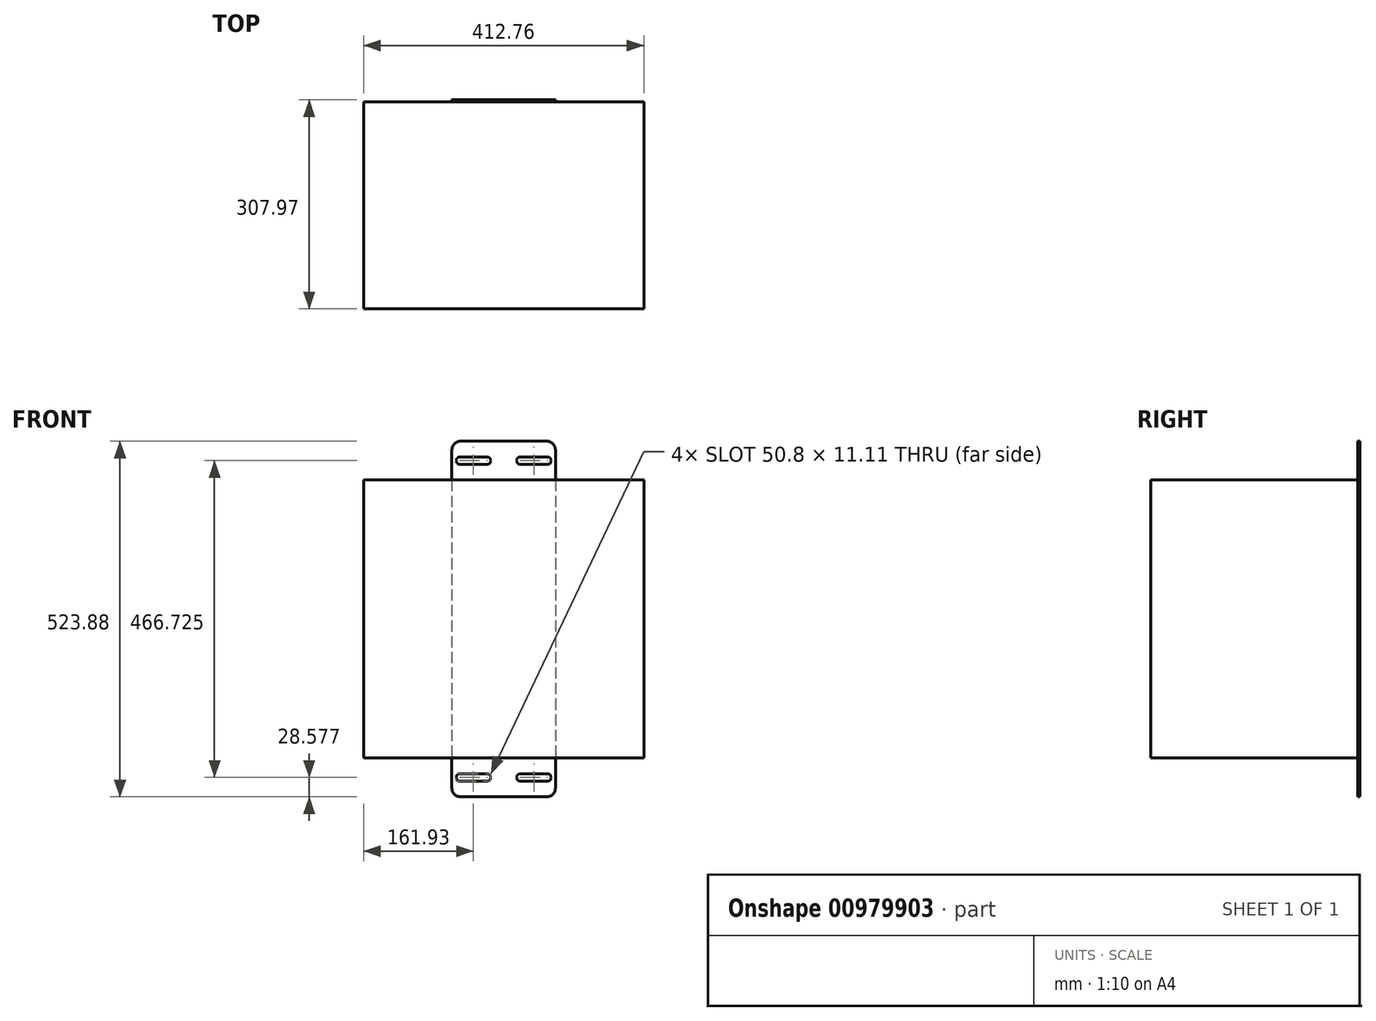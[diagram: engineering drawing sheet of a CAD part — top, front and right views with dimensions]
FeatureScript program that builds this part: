
annotation { "Feature Type Name" : "Feature", "Feature Type Description" : "" }
export const myFeature = defineFeature(function(context is Context, id is Id, definition is map)
    precondition{}
    {
        {
            var Q0;
            Q0=qCreatedBy(makeId("Top.planeOp"),FACE);
            var sketch = newSketch(context, id + "F0", { "sketchPlane" : qUnion([Q0])});
            skLineSegment(sketch, "E0.bottom", {"start": v(206.38, 152.4) * mm, "end": v(-206.38, 152.4) * mm});
            skLineSegment(sketch, "E0.top", {"start": v(206.38, -152.4) * mm, "end": v(-206.38, -152.4) * mm});
            skLineSegment(sketch, "E0.left", {"start": v(206.38, 152.4) * mm, "end": v(206.38, -152.4) * mm});
            skLineSegment(sketch, "E0.right", {"start": v(-206.38, 152.4) * mm, "end": v(-206.38, -152.4) * mm});
            skPoint(sketch, "E0.middle", {"position": v(0, 0) * mm});
            skSolve(sketch);
        }
        {
            var Q0;
            Q0=qSketchRegion(id+"F0",true);
            extrude(context, id + "F1", {"entities" : qUnion([Q0]), "depth" : 409.57 * mm, "offsetDistance" : 25.4 * mm, "symmetric" : true});
        }
        {
            var Q0;
            Q0=makeQuery(id+"F1.opExtrude","SWEPT_FACE",FACE,{"disambiguationData":[OSD([sQuery(id+"F0.wireOp",EDGE,"E0.bottom")])]});
            var sketch = newSketch(context, id + "F2", { "sketchPlane" : qUnion([Q0])});
            skLineSegment(sketch, "E1.bottom", {"start": v(63.5, 261.94) * mm, "end": v(-63.5, 261.94) * mm});
            skLineSegment(sketch, "E1.top", {"start": v(63.5, -261.94) * mm, "end": v(-63.5, -261.94) * mm});
            skLineSegment(sketch, "E1.left", {"start": v(76.2, 249.24) * mm, "end": v(76.2, -249.24) * mm});
            skLineSegment(sketch, "E1.right", {"start": v(-76.2, 249.24) * mm, "end": v(-76.2, -249.24) * mm});
            skPoint(sketch, "E1.middle", {"position": v(0, 0) * mm});
            skLineSegment(sketch, "E2", {"start": v(-76.2, 0) * mm, "end": v(76.2, 0) * mm, "construction": true});
            skLineSegment(sketch, "E3.0", {"start": v(-206.38, 204.79) * mm, "end": v(206.38, 204.79) * mm, "construction": true});
            skPoint(sketch, "E4.visualSharp", {"position": v(-76.2, 261.94) * mm});
            skArc(sketch, "E4.filletArc", {"start": v(-63.5, 261.94) * mm, "mid": v(-72.48, 258.22) * mm, "end": v(-76.2, 249.24) * mm});
            skPoint(sketch, "E5.visualSharp", {"position": v(76.2, 261.94) * mm});
            skArc(sketch, "E5.filletArc", {"start": v(76.2, 249.24) * mm, "mid": v(72.48, 258.22) * mm, "end": v(63.5, 261.94) * mm});
            skPoint(sketch, "E6.visualSharp", {"position": v(-76.2, -261.94) * mm});
            skArc(sketch, "E6.filletArc", {"start": v(-76.2, -249.24) * mm, "mid": v(-72.48, -258.22) * mm, "end": v(-63.5, -261.94) * mm});
            skPoint(sketch, "E7.visualSharp", {"position": v(76.2, -261.94) * mm});
            skArc(sketch, "E7.filletArc", {"start": v(63.5, -261.94) * mm, "mid": v(72.48, -258.22) * mm, "end": v(76.2, -249.24) * mm});
            skLineSegment(sketch, "E8", {"start": v(0, 261.94) * mm, "end": v(0, 204.79) * mm, "construction": true});
            skLineSegment(sketch, "E9", {"start": v(-76.2, 233.36) * mm, "end": v(76.2, 233.36) * mm, "construction": true});
            skPoint(sketch, "E9.startSnap0", {"position": v(0, 233.36) * mm});
            skLineSegment(sketch, "E10.bottom", {"start": v(64.3, 238.92) * mm, "end": v(24.6, 238.92) * mm});
            skLineSegment(sketch, "E10.top", {"start": v(64.3, 227.8) * mm, "end": v(24.6, 227.8) * mm});
            skLineSegment(sketch, "E10.left", {"start": v(64.3, 238.92) * mm, "end": v(64.3, 227.8) * mm, "construction": true});
            skLineSegment(sketch, "E10.right", {"start": v(24.6, 238.92) * mm, "end": v(24.6, 227.8) * mm, "construction": true});
            skPoint(sketch, "E10.middle", {"position": v(44.45, 233.36) * mm});
            skLineSegment(sketch, "E11.bottom", {"start": v(-24.6, 238.92) * mm, "end": v(-64.3, 238.92) * mm});
            skLineSegment(sketch, "E11.top", {"start": v(-24.6, 227.8) * mm, "end": v(-64.3, 227.8) * mm});
            skLineSegment(sketch, "E11.left", {"start": v(-24.6, 238.92) * mm, "end": v(-24.6, 227.8) * mm, "construction": true});
            skLineSegment(sketch, "E11.right", {"start": v(-64.3, 238.92) * mm, "end": v(-64.3, 227.8) * mm, "construction": true});
            skPoint(sketch, "E11.middle", {"position": v(-44.45, 233.36) * mm});
            skArc(sketch, "E12", {"start": v(-64.3, 238.92) * mm, "mid": v(-69.85, 233.36) * mm, "end": v(-64.3, 227.8) * mm});
            skArc(sketch, "E13", {"start": v(-24.6, 227.8) * mm, "mid": v(-19.05, 233.36) * mm, "end": v(-24.6, 238.92) * mm});
            skArc(sketch, "E14", {"start": v(24.6, 238.92) * mm, "mid": v(19.05, 233.36) * mm, "end": v(24.6, 227.8) * mm});
            skArc(sketch, "E15", {"start": v(64.3, 227.8) * mm, "mid": v(69.85, 233.36) * mm, "end": v(64.3, 238.92) * mm});
            skLineSegment(sketch, "E16.MirrorCS", {"start": v(64.3, -227.8) * mm, "end": v(24.6, -227.8) * mm});
            skArc(sketch, "E17.MirrorCS", {"start": v(64.3, -227.8) * mm, "mid": v(69.85, -233.36) * mm, "end": v(64.3, -238.92) * mm});
            skLineSegment(sketch, "E18.MirrorCS", {"start": v(64.3, -238.92) * mm, "end": v(24.6, -238.92) * mm});
            skArc(sketch, "E19.MirrorCS", {"start": v(24.6, -238.92) * mm, "mid": v(19.05, -233.36) * mm, "end": v(24.6, -227.8) * mm});
            skArc(sketch, "E20.MirrorCS", {"start": v(-24.6, -227.8) * mm, "mid": v(-19.05, -233.36) * mm, "end": v(-24.6, -238.92) * mm});
            skLineSegment(sketch, "E21.MirrorCS", {"start": v(-24.6, -238.92) * mm, "end": v(-64.3, -238.92) * mm});
            skArc(sketch, "E22.MirrorCS", {"start": v(-64.3, -238.92) * mm, "mid": v(-69.85, -233.36) * mm, "end": v(-64.3, -227.8) * mm});
            skLineSegment(sketch, "E23.MirrorCS", {"start": v(-24.6, -227.8) * mm, "end": v(-64.3, -227.8) * mm});
            skLineSegment(sketch, "E24.MirrorCS", {"start": v(-64.3, -238.92) * mm, "end": v(-64.3, -227.8) * mm, "construction": true});
            skLineSegment(sketch, "E25.MirrorCS", {"start": v(-24.6, -238.92) * mm, "end": v(-24.6, -227.8) * mm, "construction": true});
            skLineSegment(sketch, "E26.MirrorCS", {"start": v(24.6, -238.92) * mm, "end": v(24.6, -227.8) * mm, "construction": true});
            skLineSegment(sketch, "E27.MirrorCS", {"start": v(64.3, -238.92) * mm, "end": v(64.3, -227.8) * mm, "construction": true});
            skSolve(sketch);
        }
        {
            var Q0;
            Q0=qSketchRegion(id+"F2",true);
            extrude(context, id + "F3", {"entities" : qUnion([Q0]), "operationType" : NewBodyOperationType.ADD, "depth" : 3.17 * mm, "offsetDistance" : 25.4 * mm});
        }
    });
